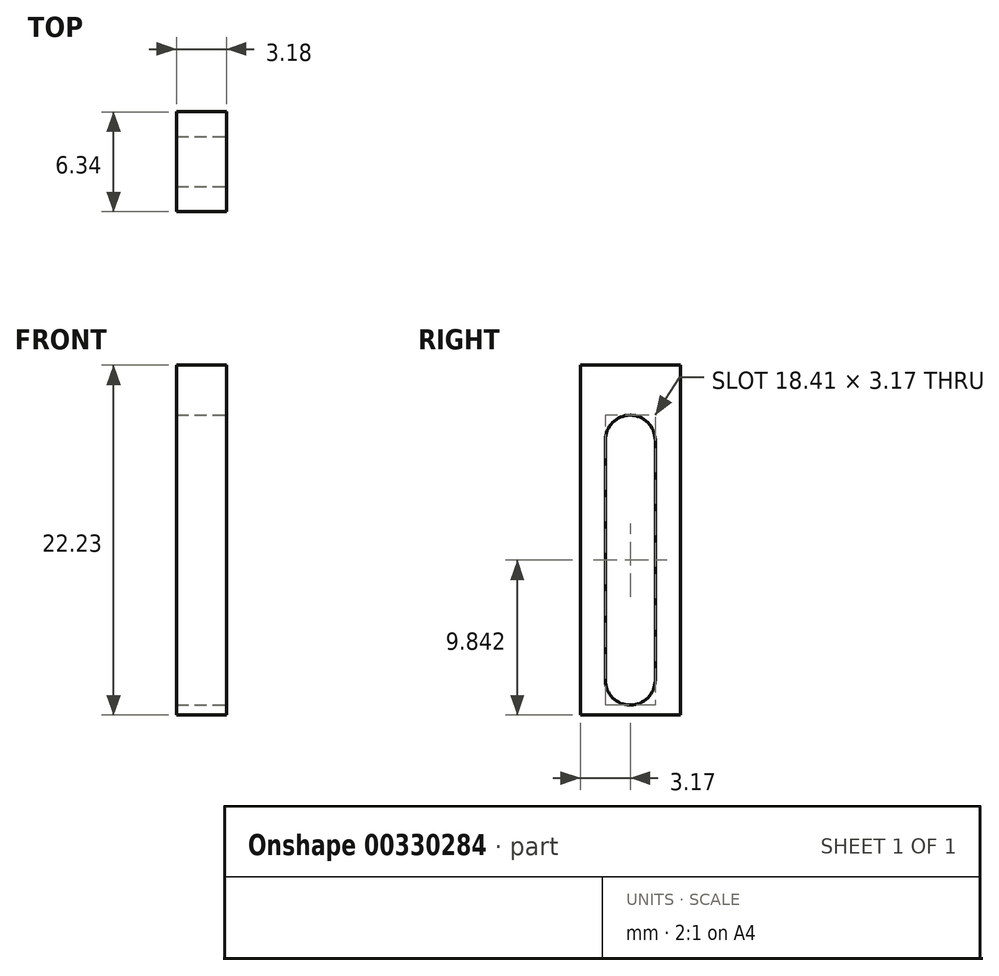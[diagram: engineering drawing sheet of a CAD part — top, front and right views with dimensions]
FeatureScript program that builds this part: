
annotation { "Feature Type Name" : "Feature", "Feature Type Description" : "" }
export const myFeature = defineFeature(function(context is Context, id is Id, definition is map)
    precondition{}
    {
        {
            var Q0;
            Q0=qCreatedBy(makeId("Right.planeOp"),FACE);
            var sketch = newSketch(context, id + "F0", { "sketchPlane" : qUnion([Q0])});
            skLineSegment(sketch, "E0", {"start": v(0, 0) * mm, "end": v(-3.18, 0) * mm});
            skLineSegment(sketch, "E1", {"start": v(-3.18, 0) * mm, "end": v(-3.18, 22.23) * mm});
            skLineSegment(sketch, "E2.MirrorCS", {"start": v(0, 0) * mm, "end": v(3.18, 0) * mm});
            skLineSegment(sketch, "E3.MirrorCS", {"start": v(3.18, 0) * mm, "end": v(3.18, 22.23) * mm});
            skLineSegment(sketch, "E4", {"start": v(-3.18, 22.23) * mm, "end": v(3.18, 22.23) * mm});
            skSolve(sketch);
        }
        {
            var Q0;
            Q0 = qSketchRegion(id + "F0", true);
            extrude(context, id + "F1", {"entities" : qUnion([Q0]), "depth" : 3.17 * mm, "symmetric" : true});
        }
        {
            var Q0;
            Q0=makeQuery(id+"F1.opExtrude","CAP_FACE",FACE,{"disambiguationData":[OSD([sQuery(id+"F0.wireOp",EDGE,"E0"),sQuery(id+"F0.wireOp",EDGE,"Dy8auA7a-qHr1-PtNs-9g8O-DiO1V9RDPuPp"),sQuery(id+"F0.wireOp",EDGE,"MESiNxAA-OQb9-nOva-wLdl-GZOzi2LoeV99"),sQuery(id+"F0.wireOp",EDGE,"E1"),sQuery(id+"F0.wireOp",EDGE,"143c3b94-bdd6-43d7-9fa6-708ea0cf16700.MirrorCS"),sQuery(id+"F0.wireOp",EDGE,"E2.MirrorCS"),sQuery(id+"F0.wireOp",EDGE,"E3.MirrorCS"),sQuery(id+"F0.wireOp",EDGE,"143c3b94-bdd6-43d7-9fa6-708ea0cf16703.MirrorCS"),sQuery(id+"F0.wireOp",EDGE,"E4")])],"isStart":false});
            var sketch = newSketch(context, id + "F2", { "sketchPlane" : qUnion([Q0])});
            skLineSegment(sketch, "E5", {"start": v(-1.59, 17.46) * mm, "end": v(-1.59, 2.22) * mm});
            skLineSegment(sketch, "E6", {"start": v(1.59, 17.46) * mm, "end": v(1.59, 2.22) * mm});
            skArc(sketch, "E7", {"start": v(1.59, 17.46) * mm, "mid": v(0, 19.05) * mm, "end": v(-1.59, 17.46) * mm});
            skPoint(sketch, "E8.orphan", {"position": v(1.59, 19.11) * mm});
            skPoint(sketch, "E9.orphan", {"position": v(-1.59, 19.11) * mm});
            skArc(sketch, "E10", {"start": v(-1.59, 2.22) * mm, "mid": v(0, 0.64) * mm, "end": v(1.59, 2.22) * mm});
            skPoint(sketch, "E11.orphan", {"position": v(-1.59, 0.13) * mm});
            skPoint(sketch, "E12.orphan", {"position": v(1.59, 0.13) * mm});
            skSolve(sketch);
        }
        {
            var Q0;
            Q0 = qSketchRegion(id + "F2", true);
            extrude(context, id + "F3", {"entities" : qUnion([Q0]), "operationType" : NewBodyOperationType.REMOVE, "endBound" : BoundingType.THROUGH_ALL, "oppositeDirection" : true, "depth" : 25.4 * mm});
        }
    });
